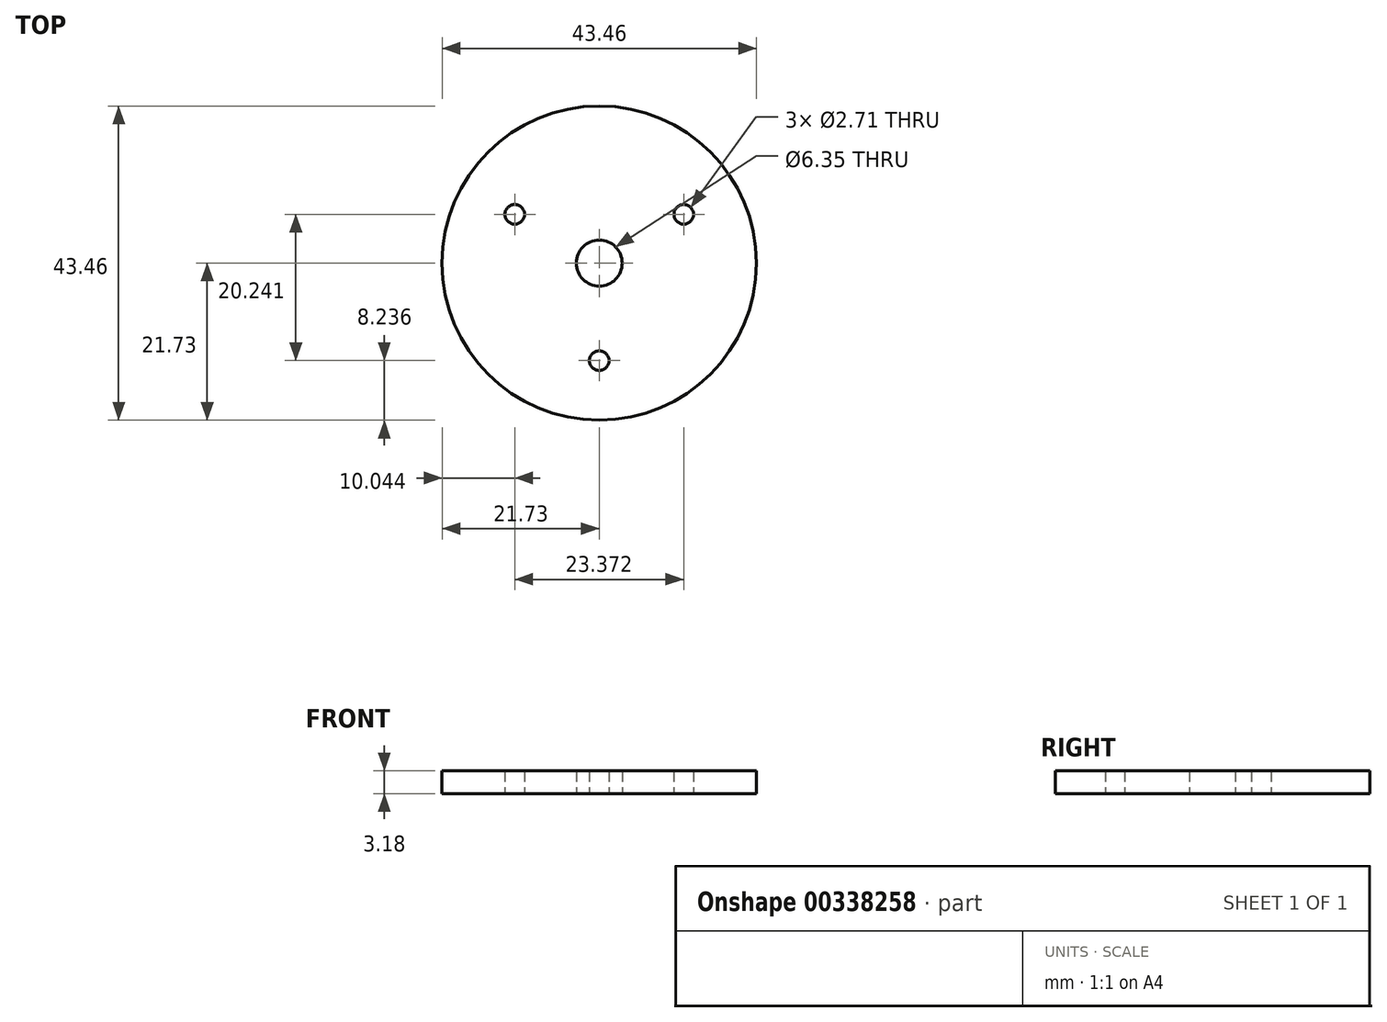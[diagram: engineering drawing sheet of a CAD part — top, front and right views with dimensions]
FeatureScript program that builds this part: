
annotation { "Feature Type Name" : "Feature", "Feature Type Description" : "" }
export const myFeature = defineFeature(function(context is Context, id is Id, definition is map)
    precondition{}
    {
        {
            var Q0;
            Q0=qCreatedBy(makeId("Top.planeOp"),FACE);
            var sketch = newSketch(context, id + "F0", { "sketchPlane" : qUnion([Q0])});
            skCircle(sketch, "E0", {"center": v(0, 0) * mm, "radius": 9.52 * mm, "construction": true});
            skCircle(sketch, "E1", {"center": v(0, 0) * mm, "radius": 21.73 * mm});
            skLineSegment(sketch, "E2", {"start": v(0, 0) * mm, "end": v(0, -13.5) * mm, "construction": true});
            skLineSegment(sketch, "E3", {"start": v(0, -13.5) * mm, "end": v(11.69, 6.75) * mm, "construction": true});
            skLineSegment(sketch, "E4", {"start": v(11.69, 6.75) * mm, "end": v(0, 0) * mm, "construction": true});
            skLineSegment(sketch, "E5", {"start": v(0, 0) * mm, "end": v(-11.69, 6.75) * mm, "construction": true});
            skLineSegment(sketch, "E6", {"start": v(-11.69, 6.75) * mm, "end": v(0, -13.5) * mm, "construction": true});
            skLineSegment(sketch, "E7", {"start": v(-11.69, 6.75) * mm, "end": v(11.69, 6.75) * mm, "construction": true});
            skCircle(sketch, "E8", {"center": v(0, -13.5) * mm, "radius": 3.97 * mm, "construction": true});
            skCircle(sketch, "E9", {"center": v(-11.69, 6.75) * mm, "radius": 1.35 * mm});
            skCircle(sketch, "E10", {"center": v(11.69, 6.75) * mm, "radius": 1.35 * mm});
            skCircle(sketch, "E11", {"center": v(0, -13.5) * mm, "radius": 1.35 * mm});
            skCircle(sketch, "E12", {"center": v(0, 0) * mm, "radius": 3.18 * mm});
            skSolve(sketch);
        }
        {
            var Q0;
            Q0=qSketchRegion(id+"F0",true);
            extrude(context, id + "F1", {"entities" : qUnion([Q0]), "depth" : 3.17 * mm});
        }
    });
